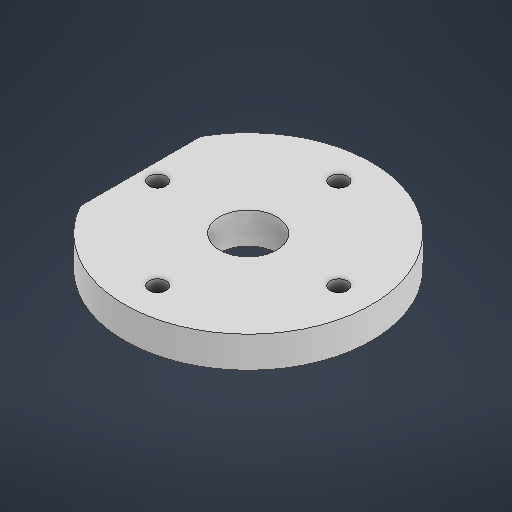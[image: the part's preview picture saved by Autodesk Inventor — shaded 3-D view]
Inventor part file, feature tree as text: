
AUTODESK INVENTOR PART (.ipt)
format: ipt  version: 2025 (Build 290162000, 162)  size: 248,832 bytes
history: native  units: in
note: dims shown in document units (in); Inventor stores cm internally (conversion verified against a paired STEP export)
features: sketch x6, extrude x4
ambient origin geometry x8: Origin, YZ Plane, XZ Plane, XY Plane, X Axis, Y Axis, Z Axis, Center Point
bodies: Solid1 (feature_tree)
feature tree (10):
  extrude  "Extrusion1"  Depth=0.7874in
  extrude  "Extrusion3"  Depth=2.2835in
  extrude  "Extrusion4"  Depth=0.3937in TaperAngle=0.0deg
  extrude  "Extrusion5"  TaperAngle=0.0deg  [1 undecoded]
  sketch  "Sketch1"  dims[d0=3.1102in d1=0.7874in]
  sketch  "Sketch Circular Pattern1"  dims[d2=2.2835in d3=0.2165in]
  sketch  "Sketch3"  dims[d4=1.5748in d6=360.0deg d8=0.3937in d9=0.0in]
  sketch  "Sketch4"  dims[d21=0.725in]
  sketch  "Sketch5"  dims[d22=0.1181in d23=0.0in d25=1.5748in d27=360.0deg d29=0.1969in d30=0.0in d33=0.0197in d34=0.0344in d35=0.0197in d36=0.0344in]
  sketch  "Sketch Circular Pattern3"  dims[d18=0.1969in d19=0.0in d20=0.0in]
note: 1 required parameter value undecoded (feature->parameter linkage not recoverable at this tier; creation-order binding heuristic only, values carry confidence <= 0.55)
